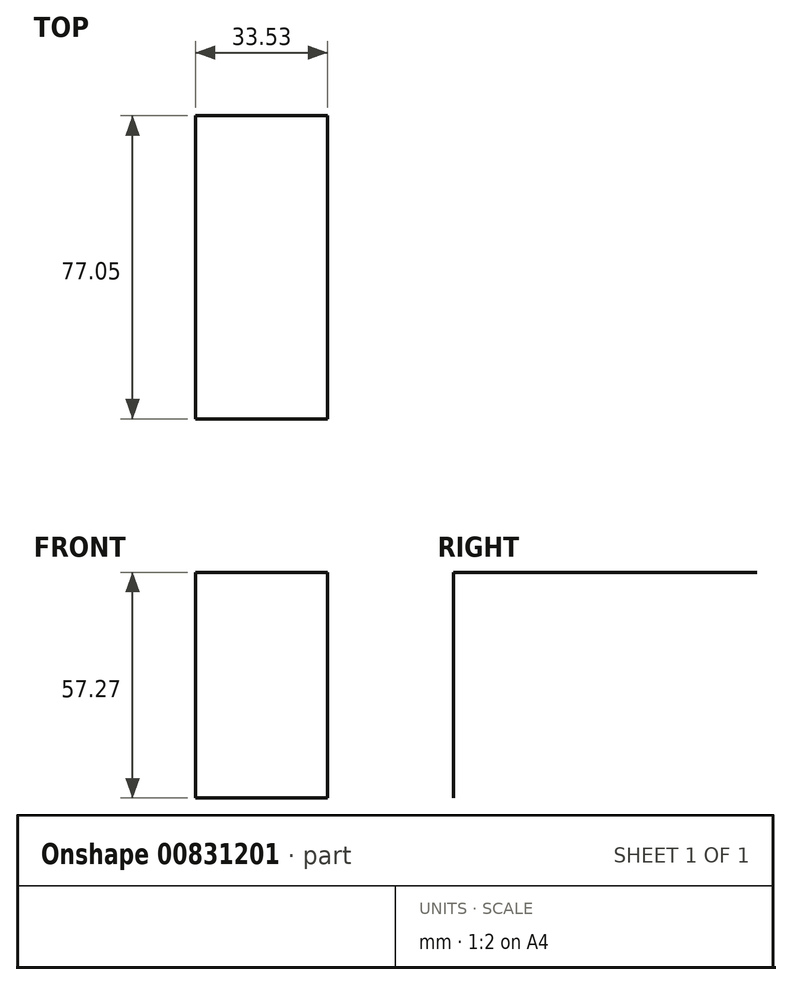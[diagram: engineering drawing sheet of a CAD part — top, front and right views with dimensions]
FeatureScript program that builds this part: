
annotation { "Feature Type Name" : "Feature", "Feature Type Description" : "" }
export const myFeature = defineFeature(function(context is Context, id is Id, definition is map)
    precondition{}
    {
        {
            var Q0;
            Q0=qCreatedBy(makeId("Right.planeOp"),FACE);
            var sketch = newSketch(context, id + "F0", { "sketchPlane" : qUnion([Q0])});
            skLineSegment(sketch, "E0", {"start": v(-77.05, 0) * mm, "end": v(-77.05, 57.27) * mm});
            skLineSegment(sketch, "E1", {"start": v(-77.05, 57.27) * mm, "end": v(0, 57.27) * mm});
            skLineSegment(sketch, "E2", {"start": v(0, 57.27) * mm, "end": v(0, 0) * mm});
            skLineSegment(sketch, "E3", {"start": v(0, 0) * mm, "end": v(-77.05, 0) * mm});
            skSolve(sketch);
        }
        {
            var Q0;
            Q0=sQuery(id+"F0.wireOp",EDGE,"E0");
            var Q1;
            Q1=sQuery(id+"F0.wireOp",EDGE,"E1");
            extrude(context, id + "F1", {"bodyType" : ToolBodyType.SURFACE, "surfaceEntities" : qUnion([Q0, Q1]), "oppositeDirection" : true, "depth" : 33.53 * mm, "offsetDistance" : 25.4 * mm});
        }
    });
